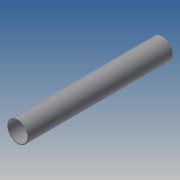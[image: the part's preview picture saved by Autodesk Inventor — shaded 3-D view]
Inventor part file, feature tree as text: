
AUTODESK INVENTOR PART (.ipt)
format: ipt  version: 2014 SP1 (Build 180222100, 222)  size: 124,416 bytes
history: native  units: in
note: dims shown in document units (in); Inventor stores cm internally (conversion verified against a paired STEP export)
features: extrude x1, sketch x1
ambient origin geometry x8: Origin, YZ Plane, XZ Plane, XY Plane, X Axis, Y Axis, Z Axis, Center Point
bodies: Solid1 (feature_tree)
feature tree (2):
  extrude  "Extrusion1"  Depth=29.5276in
  sketch  "Sketch1"  dims[d0=3.937in d1=0.175in d2=29.5276in d3=0.0in]
